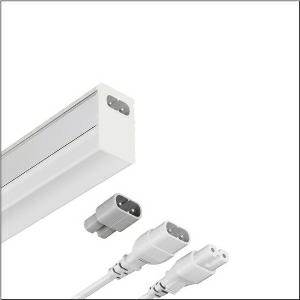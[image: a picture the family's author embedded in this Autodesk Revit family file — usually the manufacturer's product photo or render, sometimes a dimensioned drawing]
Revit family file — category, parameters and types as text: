
# Revit family: batten_41-e_51lp327km20ae
name_source: partatom
category: Lighting Fixtures
units: mm (PartAtom-declared; Revit-internal decimal feet)

## family parameters
Cut with Voids When Loaded = No
Host = Face
Light Source = No
Part Type = Normal
Room Calculation Point = No
Round Connector Dimension = Use Diameter
Shared = No

## types (1)
- --- (1 x LED, 2000 lm, 16 W, 5000K)
    Apparent Load = 16 VA
    CIE Flux Codes = 37 66 87 87 100
    Color Rendering = 80
    Color Temperature = 5000K
    Default Elevation = 1800 mm
    Description = Batten 41-E, batten luminaire, primary optical cover: cover, of PC, frosted, light emission: direct distribution, primary light characteristic: symmetric, installation type: surface-mounted, LED, rated luminous flux: 2.000lm, luminous efficacy: 125lm/W, light colour: 830/840/850, colour temperature: 3000/4000/5000K, control gear: ON/OFF, with system connector: socket, mains connection: 220..240V, AC, 50/60Hz, rated input power: 16W, housing, of aluminium, silver, length: 1.180mm, width: 25mm, height: 44mm, end cap, of PC, white, protection rating (complete): IP20, insulation class (complete): insulation class II (safety insulation), certification: CE, permissible operating ambient temperature: -20..+40°C, packaging unit: 1 piece
    Height = 44 mm
    Lamp = 1 x LED
    Lamp Light Flux = 2000 lm
    Lamp Power = 16 W
    Lamp count = 1
    Length = 1180 mm
    Luminous efficacy = 125 lm/W
    Manufacturer = Siteco
    ModVariant = No
    Model = 51LP327KM20AE
    Mounting Place = Ceiling
    Mounting Type = Surface mounted
    Number of Poles = 1
    OnlyDefault = Yes
    Power Factor = 1
    Product Name = Batten 41-E
    Product group = batten luminaire
    ProductGroupID = 303
    Protection Class = Protection class II
    Protection Degree = IP 20
    RLX_Detail_Level = 1
    RLX_Emergency_Light_Flux = 0 lm
    RLX_Emergency_Type = 0
    RLX_Emergency_Type_DB = No
    RlxData = <blob elided: 37397 chars, md5=6c3a8f5d>
    Socket = socket
    Standby Power = 0 W
    System Light Flux = 2000 lm
    System Power = 16 W
    Type Comments = individual setting: colour temperature 5000K
    Type Image = l_1007257.jpg
    URL = http://relux.com
    VarID = @adj_022782
    Voltage = 0 V
    Weight = 0.00 kg
    Width = 25 mm  [stored 0.082021 ft]

note: [stored X ft] marks values corroborated as IEEE doubles in the binary element streams (Revit-internal decimal feet)

## geometry (parser evidence)
native form markers: Blend x4, Sweep x13
no freeform markers — native parametric forms only
